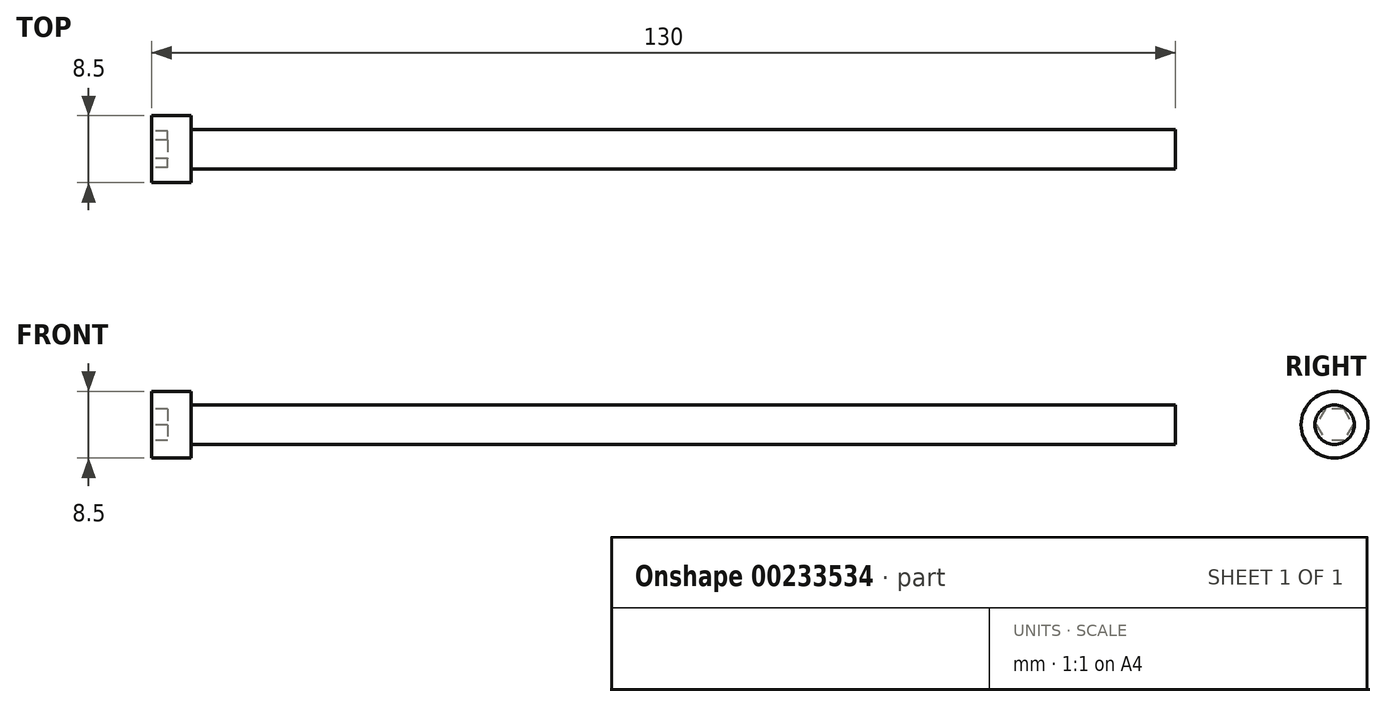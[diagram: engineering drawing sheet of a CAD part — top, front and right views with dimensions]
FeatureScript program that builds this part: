
annotation { "Feature Type Name" : "Feature", "Feature Type Description" : "" }
export const myFeature = defineFeature(function(context is Context, id is Id, definition is map)
    precondition{}
    {
        {
            var Q0;
            Q0=qCreatedBy(makeId("Top.planeOp"),FACE);
            var sketch = newSketch(context, id + "F0", { "sketchPlane" : qUnion([Q0])});
            skLineSegment(sketch, "E0", {"start": v(0, 0) * mm, "end": v(0, 4.25) * mm});
            skLineSegment(sketch, "E1", {"start": v(5, 2.5) * mm, "end": v(130, 2.5) * mm});
            skLineSegment(sketch, "E2", {"start": v(130, 2.5) * mm, "end": v(130, 0) * mm});
            skLineSegment(sketch, "E3", {"start": v(130, 0) * mm, "end": v(0, 0) * mm});
            skLineSegment(sketch, "E4", {"start": v(0, 4.25) * mm, "end": v(5, 4.25) * mm});
            skLineSegment(sketch, "E5", {"start": v(5, 4.25) * mm, "end": v(5, 2.5) * mm});
            skSolve(sketch);
        }
        {
            var Q0;
            Q0=makeQuery(id+"F0.imprint","IMPRINT",FACE,{"disambiguationData":[TD([[makeQuery(id+"F0.imprint","IMPRINT",EDGE,{"derivedFrom":sQuery(id+"F0.wireOp",EDGE,"E0")}),-1.0]])]});
            var Q1;
            Q1=sQuery(id+"F0.wireOp",EDGE,"E3");
            revolve(context, id + "F1", {"surfaceOperationType" : NewSurfaceOperationType.NEW, "entities" : qUnion([Q0]), "axis" : qUnion([Q1]), "revolveType" : RevolveType.FULL});
        }
        {
            var Q0;
            Q0=makeQuery(id+"F1.opRevolve","SWEPT_FACE",FACE,{"disambiguationData":[OSD([sQuery(id+"F0.wireOp",EDGE,"E0")])]});
            var sketch = newSketch(context, id + "F2", { "sketchPlane" : qUnion([Q0])});
            skLineSegment(sketch, "E6", {"start": v(-1.15, 2) * mm, "end": v(1.15, 2) * mm});
            skLineSegment(sketch, "E7", {"start": v(1.15, 2) * mm, "end": v(2.3, 0) * mm});
            skLineSegment(sketch, "E8", {"start": v(2.3, 0) * mm, "end": v(1.15, -2) * mm});
            skLineSegment(sketch, "E9", {"start": v(-1.15, 2) * mm, "end": v(-2.3, 0) * mm});
            skLineSegment(sketch, "E10", {"start": v(-2.3, 0) * mm, "end": v(-1.15, -2) * mm});
            skLineSegment(sketch, "E11", {"start": v(-1.15, -2) * mm, "end": v(1.15, -2) * mm});
            skSolve(sketch);
        }
        {
            var Q0;
            Q0 = qSketchRegion(id + "F2", true);
            extrude(context, id + "F3", {"entities" : qUnion([Q0]), "operationType" : NewBodyOperationType.REMOVE, "oppositeDirection" : true, "depth" : 2 * mm, "offsetDistance" : 25 * mm});
        }
    });
